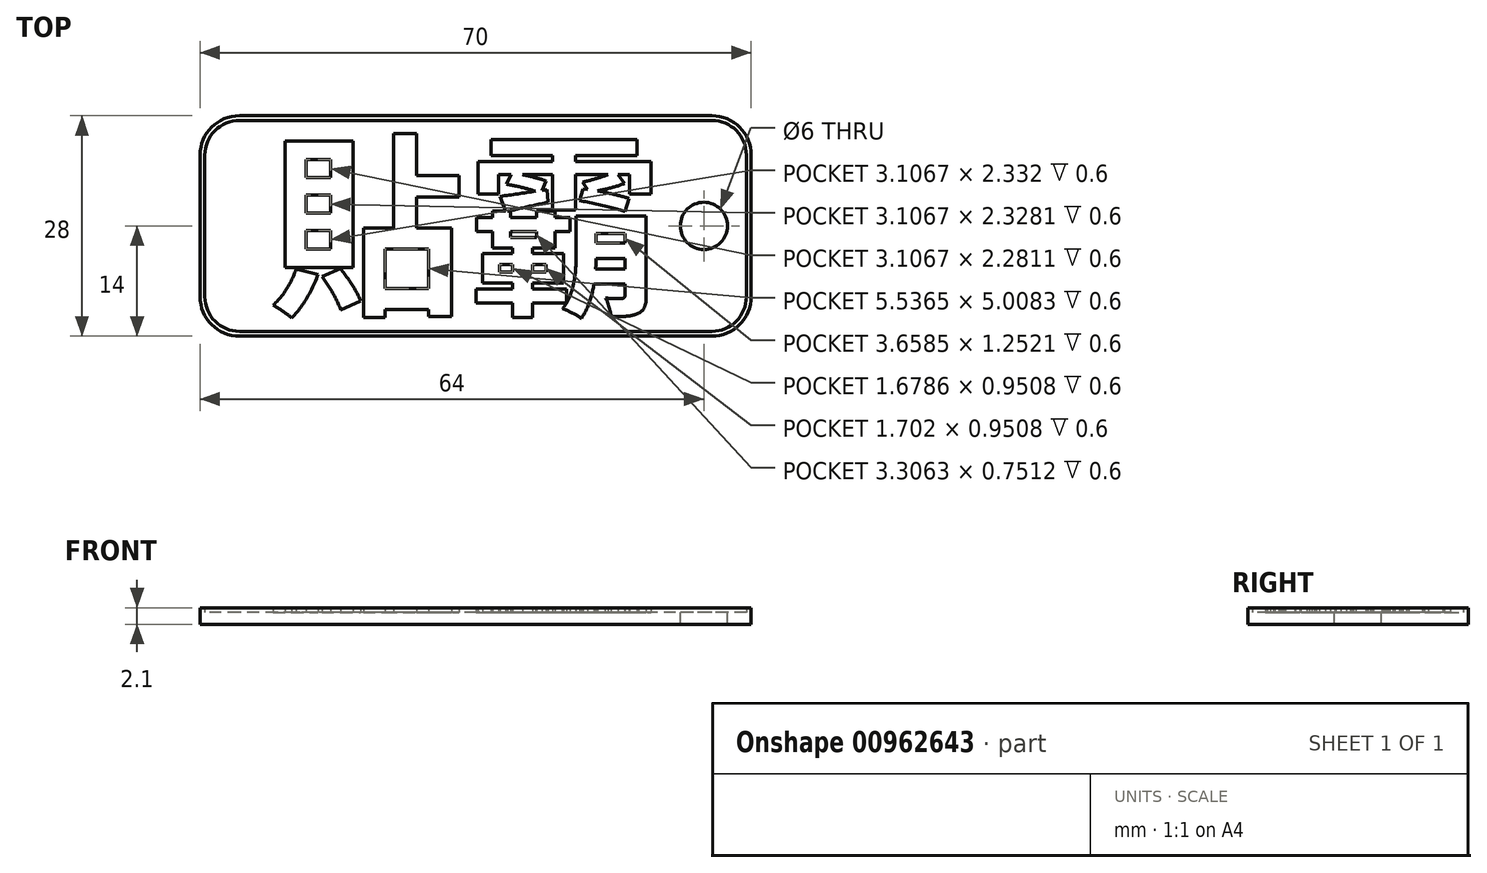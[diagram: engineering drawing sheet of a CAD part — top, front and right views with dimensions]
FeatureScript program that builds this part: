
annotation { "Feature Type Name" : "Feature", "Feature Type Description" : "" }
export const myFeature = defineFeature(function(context is Context, id is Id, definition is map)
    precondition{}
    {
        {
            var Q0;
            Q0=qCreatedBy(makeId("Top.planeOp"),FACE);
            var sketch = newSketch(context, id + "F0", { "sketchPlane" : qUnion([Q0])});
            skLineSegment(sketch, "E0.bottom", {"start": v(35, -14) * mm, "end": v(-35, -14) * mm});
            skLineSegment(sketch, "E0.top", {"start": v(35, 14) * mm, "end": v(-35, 14) * mm});
            skLineSegment(sketch, "E0.left", {"start": v(35, -14) * mm, "end": v(35, 14) * mm});
            skLineSegment(sketch, "E0.right", {"start": v(-35, -14) * mm, "end": v(-35, 14) * mm});
            skPoint(sketch, "E0.middle", {"position": v(0, 0) * mm});
            skSolve(sketch);
        }
        {
            var Q0;
            Q0 = qSketchRegion(id + "F0", true);
            extrude(context, id + "F1", {"entities" : qUnion([Q0]), "depth" : 1.5 * mm, "offsetDistance" : 25 * mm});
        }
        {
            var Q0;
            Q0=makeQuery(id+"F1.opExtrude","SWEPT_EDGE",EDGE,{"disambiguationData":[OSD([sQuery(id+"F0.wireOp",EDGE,"E0.top"),sQuery(id+"F0.wireOp",EDGE,"E0.left")])]});
            var Q1;
            Q1=makeQuery(id+"F1.opExtrude","SWEPT_EDGE",EDGE,{"disambiguationData":[OSD([sQuery(id+"F0.wireOp",EDGE,"E0.bottom"),sQuery(id+"F0.wireOp",EDGE,"E0.left")])]});
            var Q2;
            Q2=makeQuery(id+"F1.opExtrude","SWEPT_EDGE",EDGE,{"disambiguationData":[OSD([sQuery(id+"F0.wireOp",EDGE,"E0.top"),sQuery(id+"F0.wireOp",EDGE,"E0.right")])]});
            var Q3;
            Q3=makeQuery(id+"F1.opExtrude","SWEPT_EDGE",EDGE,{"disambiguationData":[OSD([sQuery(id+"F0.wireOp",EDGE,"E0.bottom"),sQuery(id+"F0.wireOp",EDGE,"E0.right")])]});
            fillet(context, id + "F2", {"entities" : qUnion([Q0, Q1, Q2, Q3]), "radius" : 5 * mm, "tangentPropagation" : true, "allowEdgeOverflow" : false});
        }
        {
            var Q0;
            Q0=makeQuery(id+"F1.opExtrude","CAP_FACE",FACE,{"disambiguationData":[OSD([sQuery(id+"F0.wireOp",EDGE,"E0.bottom"),sQuery(id+"F0.wireOp",EDGE,"E0.top"),sQuery(id+"F0.wireOp",EDGE,"E0.left"),sQuery(id+"F0.wireOp",EDGE,"E0.right")])],"isStart":false});
            var sketch = newSketch(context, id + "F3", { "sketchPlane" : qUnion([Q0])});
            skLineSegment(sketch, "E1.0.0", {"start": v(35, -9) * mm, "end": v(35, 9) * mm});
            skArc(sketch, "E1.0.1", {"start": v(35, 9) * mm, "mid": v(33.54, 12.54) * mm, "end": v(30, 14) * mm});
            skLineSegment(sketch, "E1.0.2", {"start": v(30, 14) * mm, "end": v(-30, 14) * mm});
            skArc(sketch, "E1.0.3", {"start": v(-30, 14) * mm, "mid": v(-33.54, 12.54) * mm, "end": v(-35, 9) * mm});
            skLineSegment(sketch, "E1.0.4", {"start": v(-35, 9) * mm, "end": v(-35, -9) * mm});
            skArc(sketch, "E1.0.5", {"start": v(-35, -9) * mm, "mid": v(-33.54, -12.54) * mm, "end": v(-30, -14) * mm});
            skLineSegment(sketch, "E1.0.6", {"start": v(-30, -14) * mm, "end": v(30, -14) * mm});
            skArc(sketch, "E1.0.7", {"start": v(30, -14) * mm, "mid": v(33.54, -12.54) * mm, "end": v(35, -9) * mm});
            skLineSegment(sketch, "E2.0", {"start": v(30, 13.4) * mm, "end": v(-30, 13.4) * mm});
            skArc(sketch, "E2.1", {"start": v(34.4, 9) * mm, "mid": v(33.11, 12.11) * mm, "end": v(30, 13.4) * mm});
            skArc(sketch, "E2.2", {"start": v(-30, 13.4) * mm, "mid": v(-33.11, 12.11) * mm, "end": v(-34.4, 9) * mm});
            skLineSegment(sketch, "E2.3", {"start": v(34.4, -9) * mm, "end": v(34.4, 9) * mm});
            skLineSegment(sketch, "E2.4", {"start": v(-34.4, 9) * mm, "end": v(-34.4, -9) * mm});
            skArc(sketch, "E2.5", {"start": v(-34.4, -9) * mm, "mid": v(-33.11, -12.11) * mm, "end": v(-30, -13.4) * mm});
            skLineSegment(sketch, "E2.6", {"start": v(-30, -13.4) * mm, "end": v(30, -13.4) * mm});
            skArc(sketch, "E2.7", {"start": v(30, -13.4) * mm, "mid": v(33.11, -12.11) * mm, "end": v(34.4, -9) * mm});
            skSolve(sketch);
        }
        {
            var Q0;
            Q0 = qSketchRegion(id + "F3", true);
            extrude(context, id + "F4", {"entities" : qUnion([Q0]), "operationType" : NewBodyOperationType.ADD, "depth" : .6 * mm, "offsetDistance" : 25 * mm});
        }
        {
            var Q0;
            Q0=makeQuery(id+"F1.opExtrude","CAP_FACE",FACE,{"disambiguationData":[OSD([sQuery(id+"F0.wireOp",EDGE,"E0.bottom"),sQuery(id+"F0.wireOp",EDGE,"E0.top"),sQuery(id+"F0.wireOp",EDGE,"E0.left"),sQuery(id+"F0.wireOp",EDGE,"E0.right")])],"isStart":false});
            var sketch = newSketch(context, id + "F5", { "sketchPlane" : qUnion([Q0])});
            skText(sketch, "E3", { "text": "貼霸", "fontName": "NotoSansCJKtc-Bold.otf"});
            const initialGuessF5  = {"E3": [-0.02629, -0.00946, 1, 0, 0.01803]};
            skSetInitialGuess(sketch, initialGuessF5);
            skSolve(sketch);
        }
        {
            var Q0;
            Q0 = qSketchRegion(id + "F5", true);
            extrude(context, id + "F6", {"entities" : qUnion([Q0]), "operationType" : NewBodyOperationType.ADD, "depth" : .6 * mm, "offsetDistance" : 25 * mm});
        }
        {
            var Q0;
            Q0=makeQuery(id+"F6.boolean.opBoolean","SPLIT",FACE,{"disambiguationData":[TD([makeQuery(id+"F4.opExtrude","SWEPT_FACE",FACE,{"disambiguationData":[OSD([sQuery(id+"F3.wireOp",EDGE,"E2.0")])]})])],"derivedFrom":makeQuery(id+"F1.opExtrude","CAP_FACE",FACE,{"disambiguationData":[OSD([sQuery(id+"F0.wireOp",EDGE,"E0.bottom"),sQuery(id+"F0.wireOp",EDGE,"E0.top"),sQuery(id+"F0.wireOp",EDGE,"E0.left"),sQuery(id+"F0.wireOp",EDGE,"E0.right")])],"isStart":false})});
            var sketch = newSketch(context, id + "F7", { "sketchPlane" : qUnion([Q0])});
            skCircle(sketch, "E4", {"center": v(29, 0) * mm, "radius": 3 * mm});
            skLineSegment(sketch, "E5", {"start": v(29, 0) * mm, "end": v(35, 0) * mm, "construction": true});
            skSolve(sketch);
        }
        {
            var Q0;
            Q0 = qSketchRegion(id + "F7", true);
            extrude(context, id + "F8", {"entities" : qUnion([Q0]), "operationType" : NewBodyOperationType.REMOVE, "endBound" : BoundingType.THROUGH_ALL, "oppositeDirection" : true, "depth" : 25 * mm, "offsetDistance" : 25 * mm});
        }
    });
